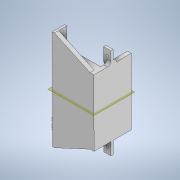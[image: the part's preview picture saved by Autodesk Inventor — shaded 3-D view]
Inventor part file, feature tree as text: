
AUTODESK INVENTOR PART (.ipt)
format: ipt  version: 2020 (Build 240168000, 168)  size: 249,856 bytes
history: native  units: mm
features: sketch x10, extrude x7, other x5, plane x5, mirror x4, hole x2, fillet x2, pattern_linear x1
ambient origin geometry x8: Origin, YZ Plane, XZ Plane, XY Plane, X Axis, Y Axis, Z Axis, Center Point
bodies: Solid1 (feature_tree)
feature tree (36):
  other  "Annotations"
  plane  "Work Plane1"
  extrude  "Extrusion1"  Depth=10.0mm TaperAngle=0.0deg
  plane  "Work Plane2"
  extrude  "Extrusion2"  Depth=30.0mm TaperAngle=0.0deg
  extrude  "Extrusion3"  Depth=86.254mm TaperAngle=0.0deg
  extrude  "Extrusion5"  Depth=8.0mm
  extrude  "Extrusion6"  Depth=240.0mm
  plane  "Work Plane3"
  mirror  "Mirror1"
  plane  "Work Plane4"
  sketch  "Sketch10"  dims[d39=20.0mm d40=240.0mm]
  extrude  "Extrusion7"  Depth=160.0mm
  pattern_linear  "Rectangular Pattern1"  Count1=4  [1 undecoded]
  hole  "Hole2"  [1 undecoded]
  mirror  "Mirror2"
  hole  "Hole3"  [1 undecoded]
  mirror  "Mirror3"
  extrude  "Extrusion9"  Depth=8.0mm
  mirror  "Mirror4"
  fillet  "Fillet1"  Radius=8.0mm
  fillet  "Fillet2"  Radius=100.0mm
  sketch  "Sketch1"  dims[d0=5.0mm d1=0.0mm d2=10.0mm d3=0.0mm]
  sketch  "Sketch3"  dims[d4=80.0mm d5=0.0mm d10=30.0mm d11=0.0mm]
  sketch  "Sketch4"  dims[d13=10.0mm d14=0.0mm d15=86.254mm d16=0.0mm]
  sketch  "Sketch6"  dims[d17=60.0mm d19=30.4mm]
  sketch  "Sketch7"  dims[d28=10.0mm d29=6.0mm d30=4.0mm d31=2.0mm d32=90.0deg d33=8.0mm d34=20.594885mm d38=15.0mm]
  sketch  "Sketch11"  dims[d41=20.0mm d42=160.0mm d43=40.0mm]
  sketch  "Sketch14"  dims[d45=6.0mm d46=6.0mm d47=4.0mm d48=2.0mm d49=90.0deg d50=8.0mm d51=20.594885mm d52=15.0mm]
  sketch  "Sketch15"  dims[d53=9.0mm d54=180.0mm d55=0.0mm]
  plane  "Work Plane5"
  sketch  "Sketch16"  dims[d56=240.0mm d57=8.0mm d58=8.0mm d44=100.0mm d21=1.0mm d22=1.0mm d23=1.0mm d24=0.15mm d25=8.0mm d26=0.375mm d27=14.3117mm]
  other  "Linear Dimension 1"
  parser-record x1  (decoder bookkeeping rows leaked as tree rows — omitted from the tree; the rows remain in map.json)
  other  "robot morango.iam"
  other  "guia:4"
note: 3 required parameter values undecoded (feature->parameter linkage not recoverable at this tier; creation-order binding heuristic only, values carry confidence <= 0.55)
note: 1 file-system path scrubbed to <path> (originals preserved in map.json)
